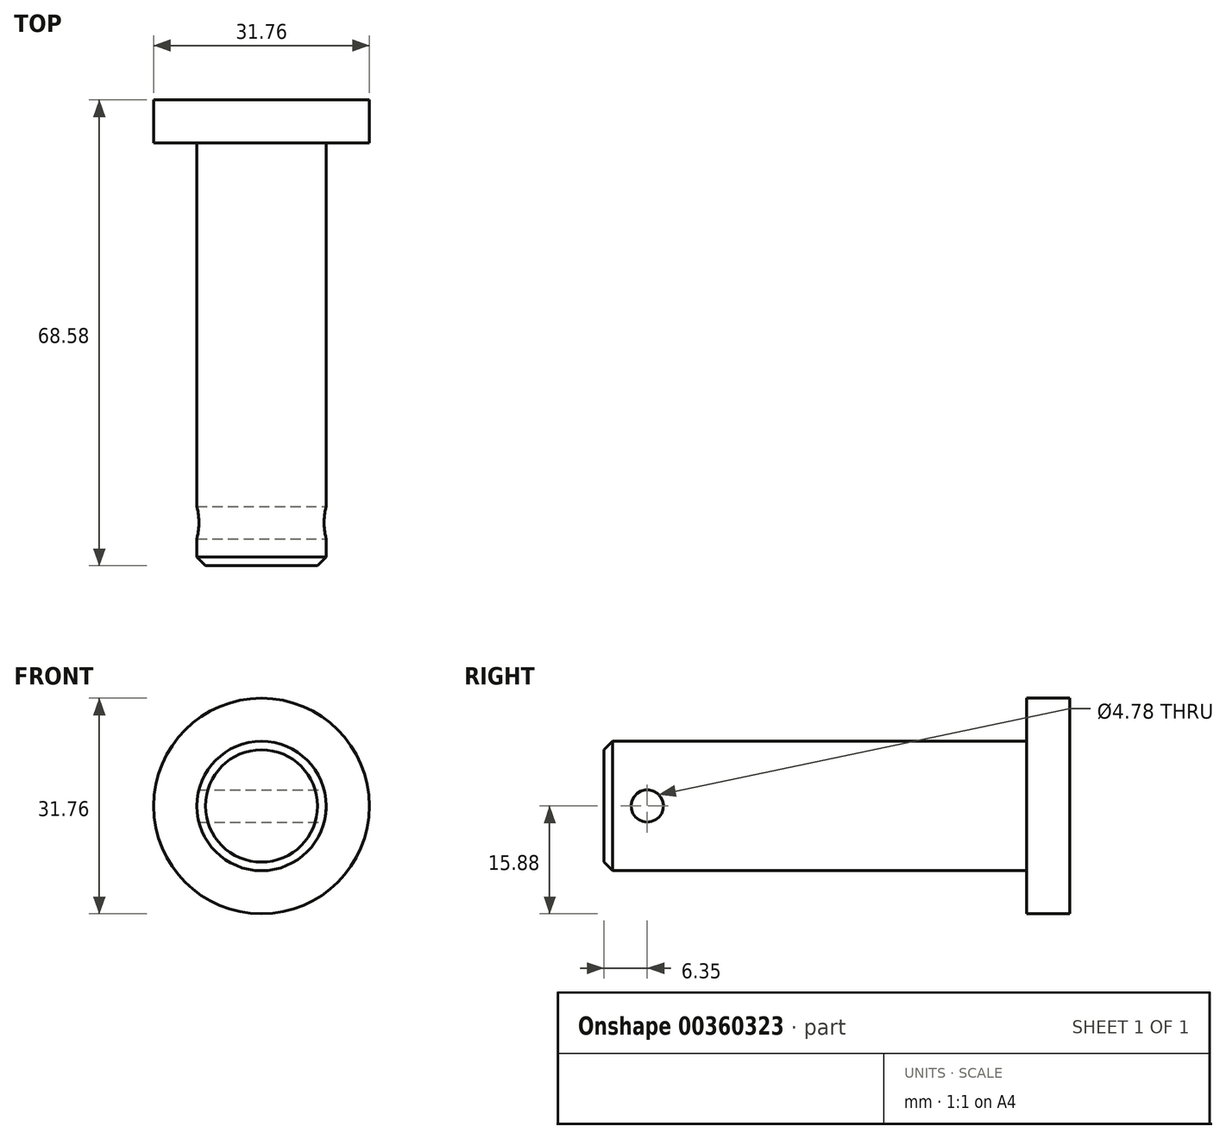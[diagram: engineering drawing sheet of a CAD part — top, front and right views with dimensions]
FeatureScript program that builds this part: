
annotation { "Feature Type Name" : "Feature", "Feature Type Description" : "" }
export const myFeature = defineFeature(function(context is Context, id is Id, definition is map)
    precondition{}
    {
        {
            var Q0;
            Q0=qCreatedBy(makeId("Front.planeOp"),FACE);
            var sketch = newSketch(context, id + "F0", { "sketchPlane" : qUnion([Q0])});
            skCircle(sketch, "E0", {"center": v(0, 0) * mm, "radius": 15.88 * mm});
            skCircle(sketch, "E1", {"center": v(0, 0) * mm, "radius": 9.53 * mm});
            skSolve(sketch);
        }
        {
            var Q0;
            Q0=makeQuery(id+"F0.imprint","IMPRINT",FACE,{"disambiguationData":[TD([[makeQuery(id+"F0.imprint","IMPRINT",EDGE,{"derivedFrom":sQuery(id+"F0.wireOp",EDGE,"E0")}),1.0]])]});
            var Q1;
            Q1=makeQuery(id+"F0.imprint","IMPRINT",FACE,{"disambiguationData":[TD([[makeQuery(id+"F0.imprint","IMPRINT",EDGE,{"derivedFrom":sQuery(id+"F0.wireOp",EDGE,"E1")}),1.0]])]});
            extrude(context, id + "F1", {"entities" : qUnion([Q0, Q1]), "oppositeDirection" : true, "depth" : 6.35 * mm});
        }
        {
            var Q0;
            Q0=makeQuery(id+"F0.imprint","IMPRINT",FACE,{"disambiguationData":[TD([[makeQuery(id+"F0.imprint","IMPRINT",EDGE,{"derivedFrom":sQuery(id+"F0.wireOp",EDGE,"E1")}),1.0]])]});
            extrude(context, id + "F2", {"entities" : qUnion([Q0]), "operationType" : NewBodyOperationType.ADD, "depth" : 62.23 * mm});
        }
        {
            var Q0;
            Q0=qCreatedBy(makeId("Right.planeOp"),FACE);
            var sketch = newSketch(context, id + "F3", { "sketchPlane" : qUnion([Q0])});
            skLineSegment(sketch, "E2", {"start": v(0, 0) * mm, "end": v(-62.23, 0) * mm, "construction": true});
            skCircle(sketch, "E3", {"center": v(-55.88, 0) * mm, "radius": 2.39 * mm});
            skSolve(sketch);
        }
        {
            var Q0;
            Q0 = qSketchRegion(id + "F3", true);
            extrude(context, id + "F4", {"entities" : qUnion([Q0]), "operationType" : NewBodyOperationType.REMOVE, "oppositeDirection" : true, "depth" : 25.4 * mm, "hasSecondDirection" : true, "secondDirectionOppositeDirection" : false, "secondDirectionDepth" : 25.4 * mm});
        }
        {
            var Q0;
            Q0=makeQuery(id+"F2.opExtrude","CAP_EDGE",EDGE,{"disambiguationData":[OSD([sQuery(id+"F0.wireOp",EDGE,"E1")])],"isStart":false});
            chamfer(context, id + "F5", {"entities" : qUnion([Q0]), "chamferType" : ChamferType.OFFSET_ANGLE, "width" : 1.27 * mm, "oppositeDirection" : false, "angle" : 45 * degree, "tangentPropagation" : true});
        }
    });
